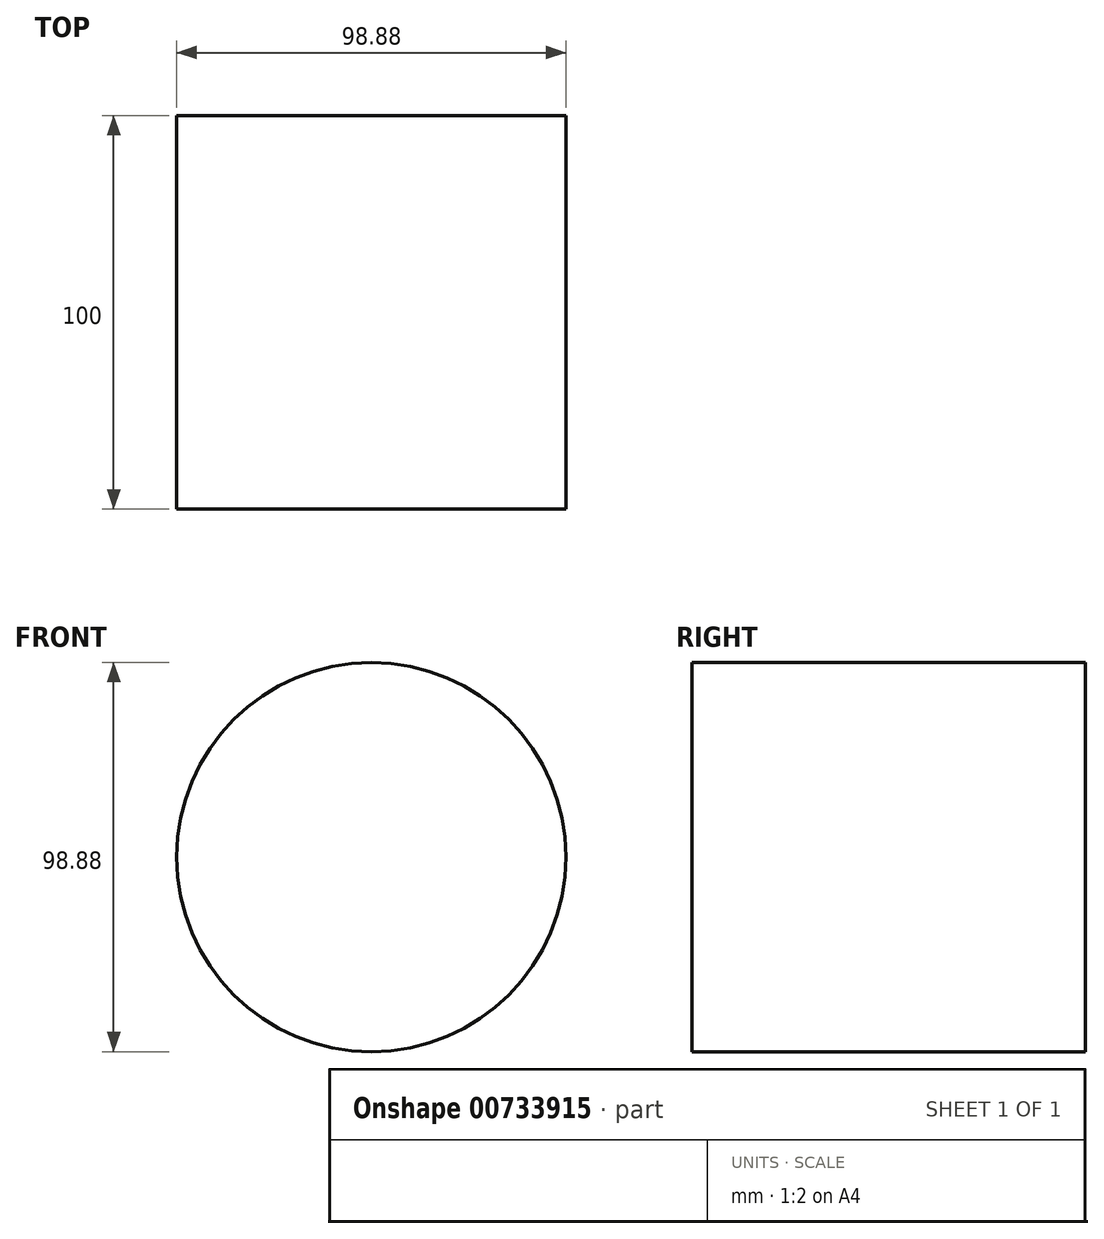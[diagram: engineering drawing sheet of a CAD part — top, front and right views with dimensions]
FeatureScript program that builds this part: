
annotation { "Feature Type Name" : "Feature", "Feature Type Description" : "" }
export const myFeature = defineFeature(function(context is Context, id is Id, definition is map)
    precondition{}
    {
        {
            var Q0;
            Q0=qCreatedBy(makeId("Front.planeOp"),FACE);
            var sketch = newSketch(context, id + "F0", { "sketchPlane" : qUnion([Q0])});
            skCircle(sketch, "E0", {"center": v(0, 0) * mm, "radius": 49.44 * mm});
            skSolve(sketch);
        }
        {
            var Q0;
            Q0 = qSketchRegion(id + "F0", true);
            extrude(context, id + "F1", {"entities" : qUnion([Q0]), "depth" : 100 * mm, "offsetDistance" : 25.4 * mm});
        }
    });
